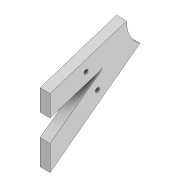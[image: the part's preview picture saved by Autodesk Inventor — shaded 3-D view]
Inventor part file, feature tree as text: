
AUTODESK INVENTOR PART (.ipt)
format: ipt  version: 2022 (Build 260153000, 153)  size: 274,944 bytes
history: native  units: mm
features: sketch x4, extrude x3, projected_geometry x1
ambient origin geometry x8: Origin, YZ Plane, XZ Plane, XY Plane, X Axis, Y Axis, Z Axis, Center Point
bodies: Solid1 (feature_tree)
feature tree (8):
  extrude  "Extrusion1"  Depth=3.9mm
  sketch  "Sketch8"  dims[d6=5.0mm d7=0.0mm d25=3.0mm]
  extrude  "Extrusion4"  Depth=5.0mm
  extrude  "Extrusion5"  Depth=59.0mm
  sketch  "Sketch1"  dims[d2=3.9mm d4=3.9mm]
  sketch  "Sketch9"  dims[d28=3.0mm d43=59.0mm]
  sketch  "Sketch10"  dims[d44=65.0mm d45=65.0mm d47=59.0mm d48=10.0mm d49=10.0mm d50=10.0mm d52=14.0mm d53=3.0mm d54=3.0mm d55=4.0mm d56=4.0mm d57=25.0mm d58=25.0mm d59=10.0mm d60=10.0mm d61=5.0mm d62=3.0mm d63=3.0mm d64=3.0mm d65=3.0mm d66=3.0mm d67=10.0mm d68=25.0mm d69=3.0mm d70=3.0mm d71=10.0mm d72=25.0mm d73=25.0mm d74=25.0mm d76=2.0mm d78=2.0mm d79=2.0mm d80=2.0mm d81=6.0mm d82=6.0mm d83=2.0mm d84=30.0mm d85=6.0mm d86=5.0mm d87=0.0mm d88=10.0mm d89=0.0mm]
  projected_geometry  "Project Cut Edges1"
